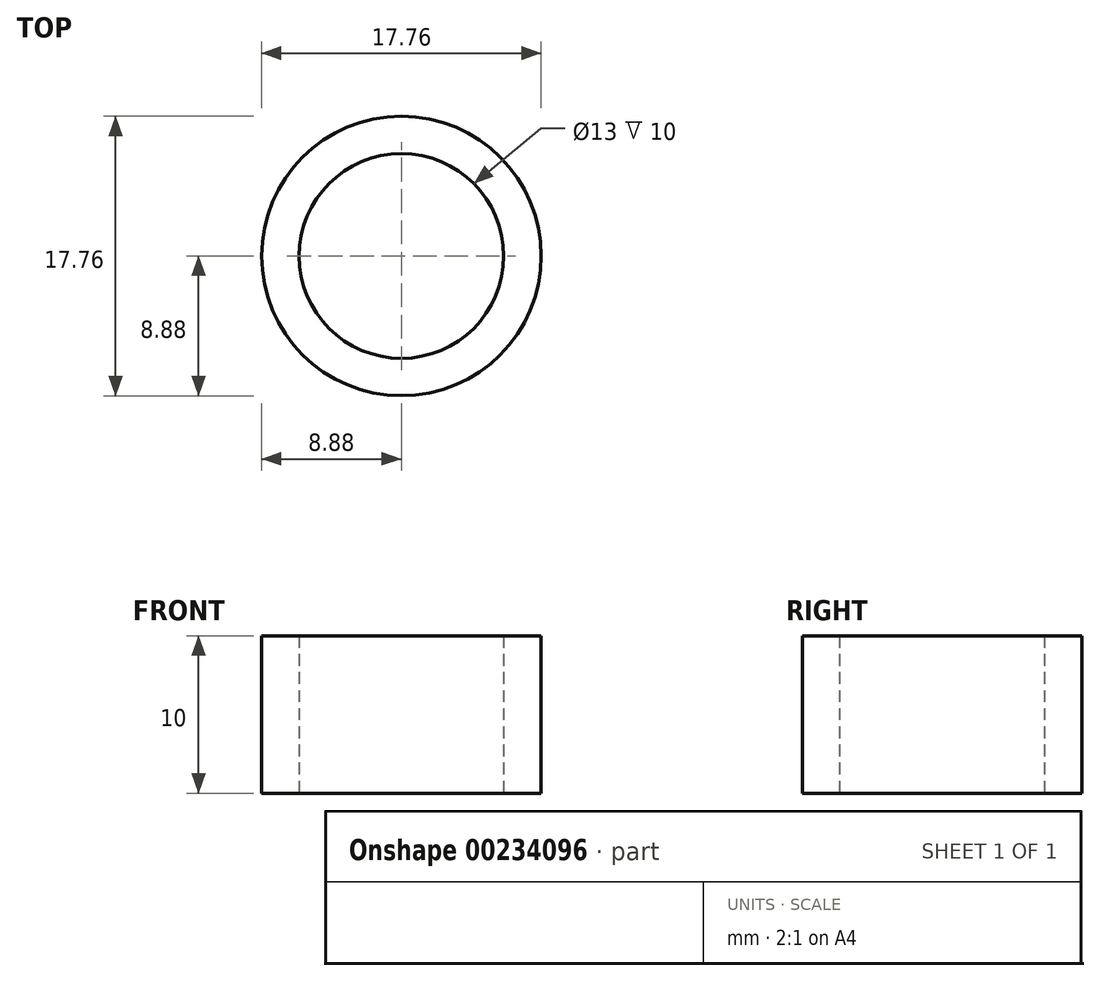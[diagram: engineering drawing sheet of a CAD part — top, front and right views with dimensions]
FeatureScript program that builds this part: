
annotation { "Feature Type Name" : "Feature", "Feature Type Description" : "" }
export const myFeature = defineFeature(function(context is Context, id is Id, definition is map)
    precondition{}
    {
        {
            var Q0;
            Q0=qCreatedBy(makeId("Top.planeOp"),FACE);
            var sketch = newSketch(context, id + "F0", { "sketchPlane" : qUnion([Q0])});
            skCircle(sketch, "E0", {"center": v(0, 0) * mm, "radius": 6.5 * mm});
            skCircle(sketch, "E1", {"center": v(0, 0) * mm, "radius": 8.88 * mm});
            skSolve(sketch);
        }
        {
            var Q0;
            Q0 = qSketchRegion(id + "F0", true);
            extrude(context, id + "F1", {"entities" : qUnion([Q0]), "depth" : 10 * mm});
        }
    });
